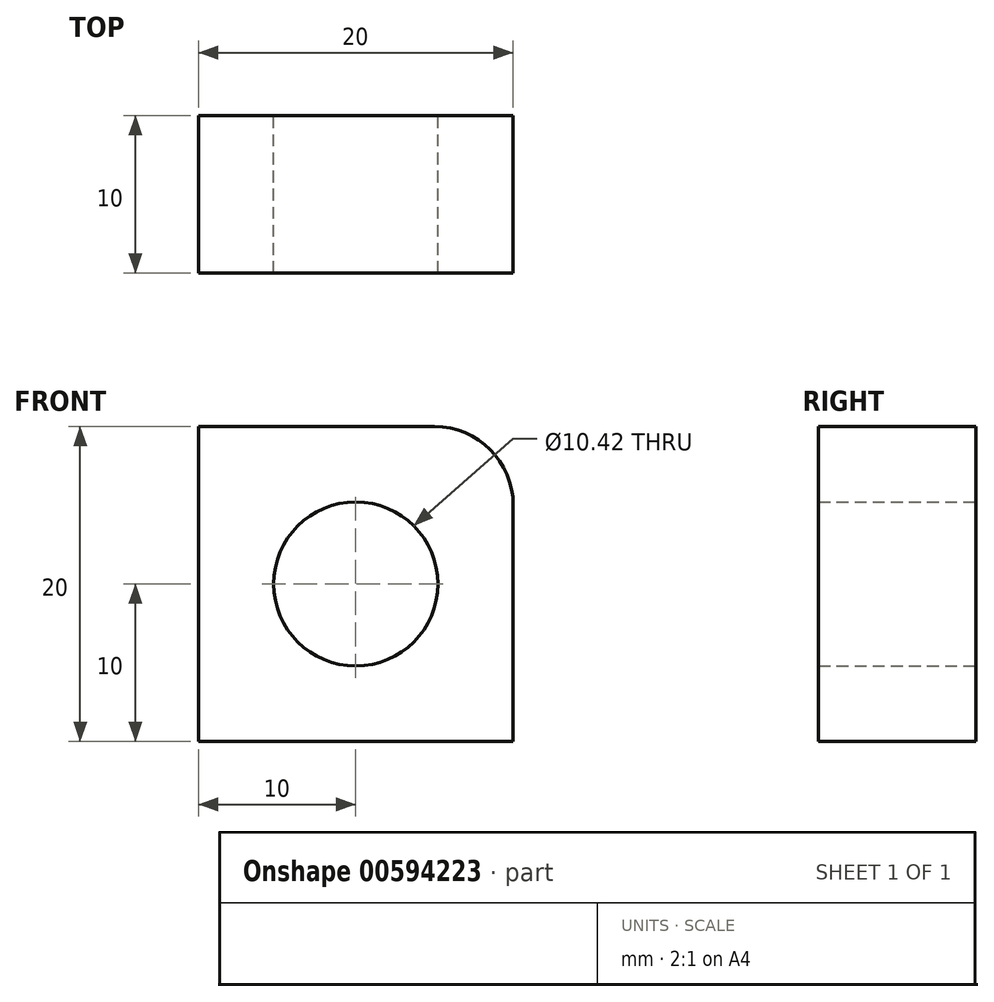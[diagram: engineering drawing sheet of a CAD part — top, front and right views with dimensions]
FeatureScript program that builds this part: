
annotation { "Feature Type Name" : "Feature", "Feature Type Description" : "" }
export const myFeature = defineFeature(function(context is Context, id is Id, definition is map)
    precondition{}
    {
        {
            var Q0;
            Q0=qCreatedBy(makeId("Front.planeOp"),FACE);
            var sketch = newSketch(context, id + "F0", { "sketchPlane" : qUnion([Q0])});
            skLineSegment(sketch, "E0.bottom", {"start": v(-10, 10) * mm, "end": v(5, 10) * mm});
            skLineSegment(sketch, "E0.top", {"start": v(-10, -10) * mm, "end": v(10, -10) * mm});
            skLineSegment(sketch, "E0.left", {"start": v(-10, 10) * mm, "end": v(-10, -10) * mm});
            skLineSegment(sketch, "E0.right", {"start": v(10, 5) * mm, "end": v(10, -10) * mm});
            skPoint(sketch, "E0.middle", {"position": v(0, 0) * mm});
            skCircle(sketch, "E1", {"center": v(0, 0) * mm, "radius": 5.21 * mm});
            skPoint(sketch, "E2.visualSharp", {"position": v(10, 10) * mm});
            skArc(sketch, "E2.filletArc", {"start": v(10, 5) * mm, "mid": v(8.54, 8.54) * mm, "end": v(5, 10) * mm});
            skSolve(sketch);
        }
        {
            var Q0;
            Q0=makeQuery(id+"F0.imprint","IMPRINT",FACE,{"disambiguationData":[TD([[makeQuery(id+"F0.imprint","IMPRINT",EDGE,{"derivedFrom":sQuery(id+"F0.wireOp",EDGE,"E0.bottom")}),-1.0]])]});
            extrude(context, id + "F1", {"entities" : qUnion([Q0]), "depth" : 10 * mm, "offsetDistance" : 25 * mm});
        }
    });
